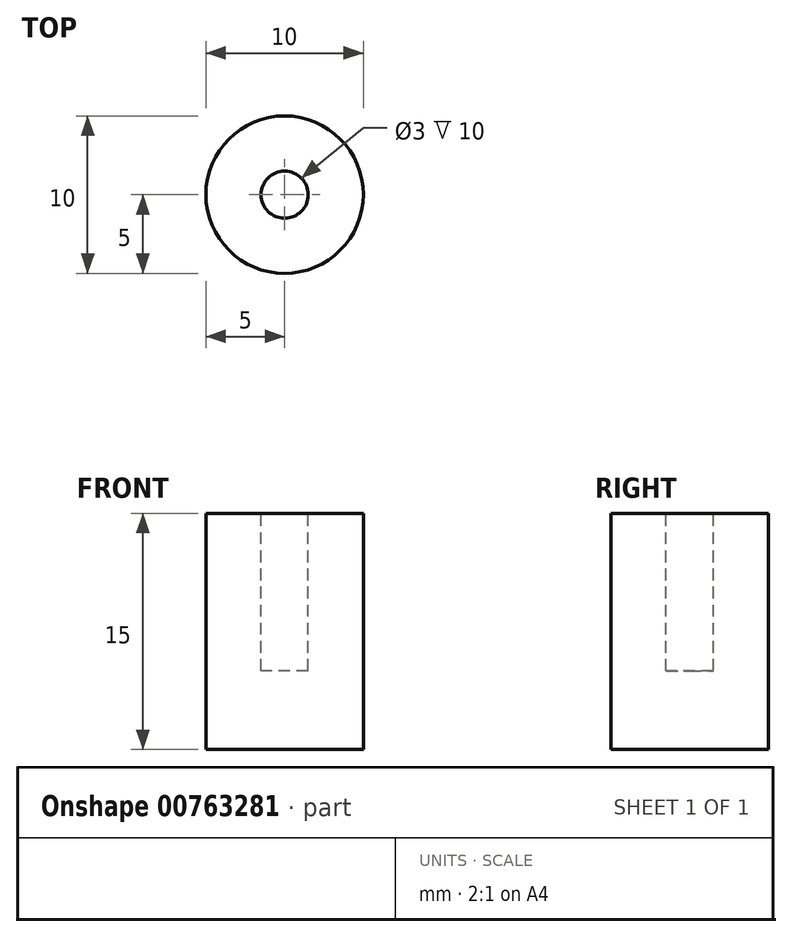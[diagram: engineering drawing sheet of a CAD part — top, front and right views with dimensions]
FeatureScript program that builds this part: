
annotation { "Feature Type Name" : "Feature", "Feature Type Description" : "" }
export const myFeature = defineFeature(function(context is Context, id is Id, definition is map)
    precondition{}
    {
        {
            var Q0;
            Q0=qCreatedBy(makeId("Top.planeOp"),FACE);
            var sketch = newSketch(context, id + "F0", { "sketchPlane" : qUnion([Q0])});
            skCircle(sketch, "E0", {"center": v(0, 0) * mm, "radius": 5 * mm});
            skCircle(sketch, "E1", {"center": v(0, 0) * mm, "radius": 1.5 * mm});
            skSolve(sketch);
        }
        {
            var Q0;
            Q0 = qSketchRegion(id + "F0", true);
            var Q1;
            Q1=makeQuery(id+"F0.imprint","IMPRINT",FACE,{"disambiguationData":[TD([[makeQuery(id+"F0.imprint","IMPRINT",EDGE,{"derivedFrom":sQuery(id+"F0.wireOp",EDGE,"E1")}),1.0]])]});
            extrude(context, id + "F1", {"entities" : qUnion([Q0, Q1]), "oppositeDirection" : true, "depth" : 15 * mm, "offsetDistance" : 25 * mm});
        }
        {
            var Q0;
            Q0=makeQuery(id+"F0.imprint","IMPRINT",FACE,{"disambiguationData":[TD([[makeQuery(id+"F0.imprint","IMPRINT",EDGE,{"derivedFrom":sQuery(id+"F0.wireOp",EDGE,"E1")}),1.0]])]});
            extrude(context, id + "F2", {"entities" : qUnion([Q0]), "operationType" : NewBodyOperationType.REMOVE, "oppositeDirection" : true, "depth" : 10 * mm, "offsetDistance" : 25 * mm});
        }
    });
